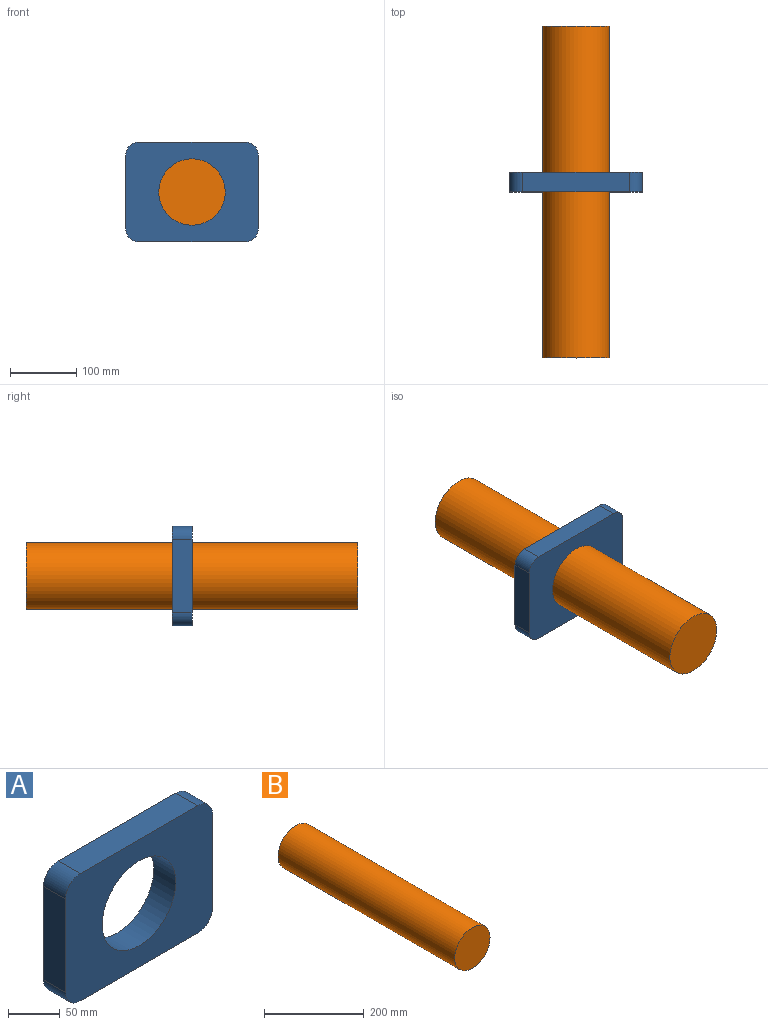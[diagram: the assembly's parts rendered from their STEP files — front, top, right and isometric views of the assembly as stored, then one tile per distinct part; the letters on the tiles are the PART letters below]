
ASSEMBLY  parts=2 mates=2
PART A: 11 faces, bbox 200x30x150 mm
  f0: plane 110x30mm, normal (1,0,0), area 3300mm2, adj f5,f6,f7,f10
  f1: plane 160x30mm, normal (0,0,1), area 4800mm2, adj f5,f6,f7,f8
  f2: plane 110x30mm, normal (-1,0,0), area 3300mm2, adj f5,f6,f8,f9
  f3: plane 160x30mm, normal (0,0,-1), area 4800mm2, adj f5,f6,f9,f10
  f4: cylinder r=50mm len=100mm, axis (0,1,0), area 9424.8mm2, adj f5,f6
  f5: plane 200x150mm, normal (0,-1,0), area 21802.7mm2, adj f0,f1,f2,f3,f4,f7,f8,f9
  f6: plane 200x150mm, normal (0,1,0), area 21802.7mm2, adj f0,f1,f2,f3,f4,f7,f8,f9
  f7: cylinder r=20mm len=30mm, axis (0,-1,0), area 942.5mm2, adj f0,f1,f5,f6
  f8: cylinder r=20mm len=30mm, axis (0,1,0), area 942.5mm2, adj f1,f2,f5,f6
  f9: cylinder r=20mm len=30mm, axis (0,-1,0), area 942.5mm2, adj f2,f3,f5,f6
  f10: cylinder r=20mm len=30mm, axis (0,1,0), area 942.5mm2, adj f0,f3,f5,f6
PART B: 3 faces, bbox 100x500x100 mm
  f0: cylinder r=50mm len=500mm, axis (0,1,0), area 157079.6mm2, adj f1,f2
  f1: plane 100x100mm, normal (0,-1,0), area 7854mm2, adj f0
  f2: plane 100x100mm, normal (0,1,0), area 7854mm2, adj f0
PLACE A t=(-60.37,210.46,-52.03)mm
PLACE B t=(-60.37,195.46,-52.03)mm
MATE slider B.f0 <-> A.f4  axis (0,-1,0) through (-60.37,-54.54,-52.03)mm
MATE fastened A.f4 <-> B.f0  axis (0,-1,0) through (-60.37,195.46,-52.03)mm
